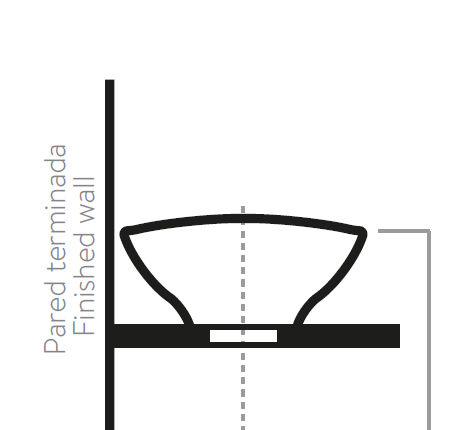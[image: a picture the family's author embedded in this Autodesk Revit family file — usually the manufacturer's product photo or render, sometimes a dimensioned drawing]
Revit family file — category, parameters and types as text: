
# Revit family: O14621031_Lavamanos Ravenna Vessel
name_source: partatom
category: Plumbing Fixtures
units: mm (PartAtom-declared; Revit-internal decimal feet)

## family parameters
Cut with Voids When Loaded = No
Host = Face
OmniClass Number = 23.31.13.11
OmniClass Title = Single Sinks
Part Type = Normal
Room Calculation Point = No
Round Connector Dimension = Use Diameter
Shared = No

## types (1)
- O14621031_Lavamanos Ravenna Vessel
    Alto = 140 mm  [stored 0.459318 ft]
    Ancho = 400 mm  [stored 1.31234 ft]
    Colección = Lavamanos 2007
    Creado por = BIMBAU
    Default Elevation = 1219 mm
    Description = Nuestro lavamanos para sobreponer tipo Vessel es de práctico tamaño porque además se recomienda instalar con griferías a la pared o de mesón altas.
    Fecha de creación = 07/04/2021
    Forma = Ovalado
    Garantía = Garantía CORONA limitada de por vida.
    Manufacturer = Corona
    Material = Corona_Porcelana_Sanitaria
    Material 2 = Corona_Acero inoxidable
    Model = Ravenna
    Normatividad = NTC 920 y ASME/ANSI A112.19.2.
    Pozo = 13 3/8¨ x 15 3/8¨ x 5 1/8 (34 cm x 39 cm x 13 cm) de longitud.
    Profundidad = 330 mm  [stored 1.08268 ft]
    Referencia = O14621031
    Resistencia al rayado = Alta resistencia al rayado y cambios de temperatura
    URL = https://corona.co
    Uso = Residencial

note: [stored X ft] marks values corroborated as IEEE doubles in the binary element streams (Revit-internal decimal feet)

## geometry (parser evidence)
native form markers: Sweep x7
no freeform markers — native parametric forms only
